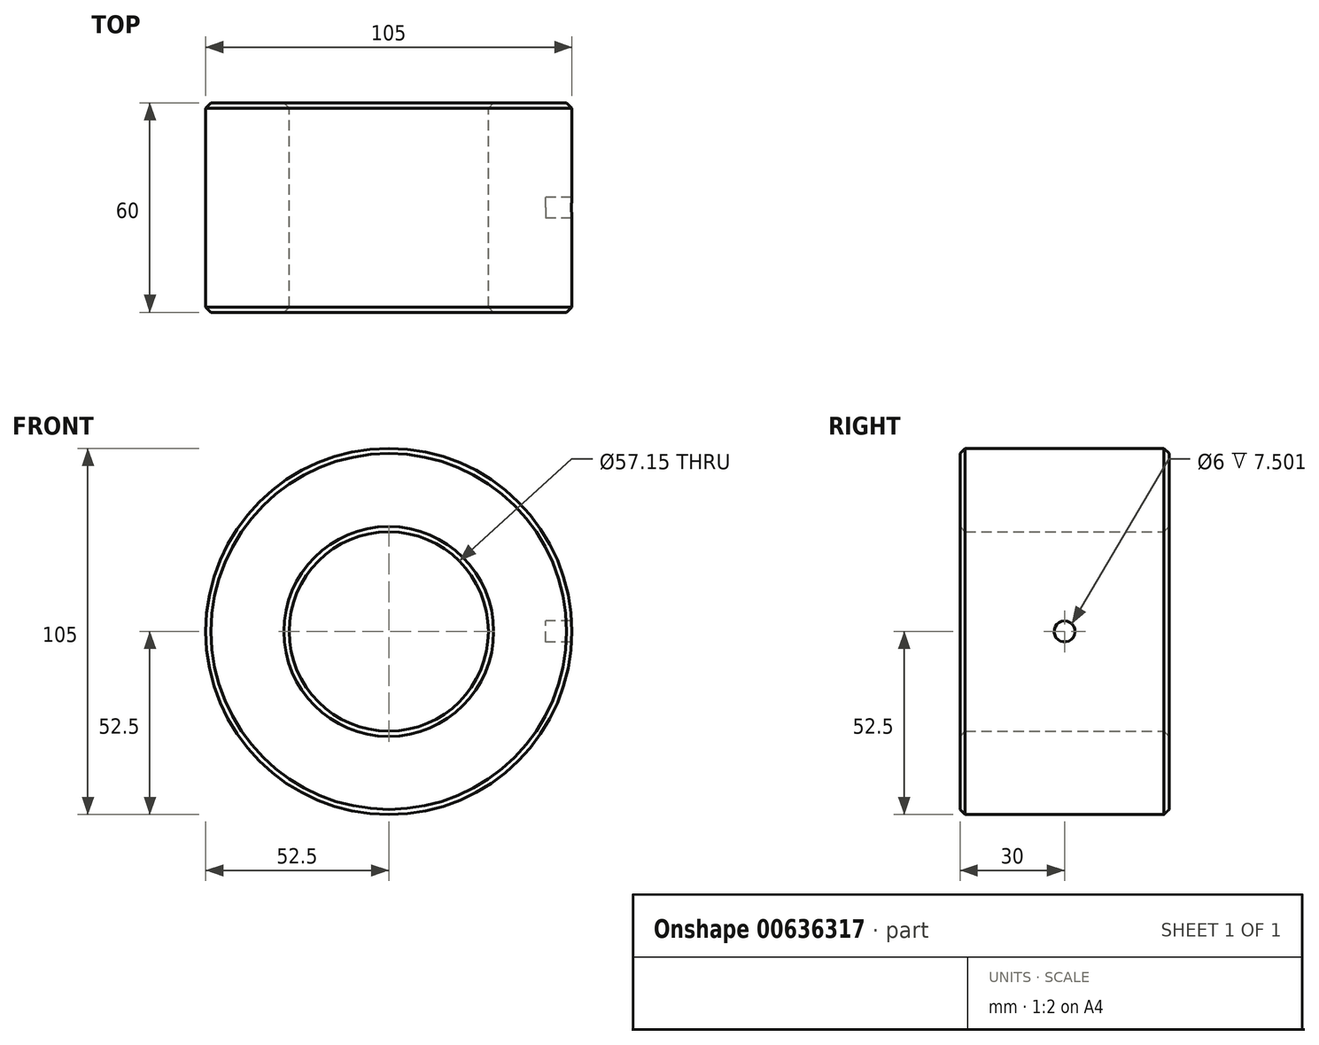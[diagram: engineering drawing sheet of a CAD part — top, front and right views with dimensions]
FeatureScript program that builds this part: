
annotation { "Feature Type Name" : "Feature", "Feature Type Description" : "" }
export const myFeature = defineFeature(function(context is Context, id is Id, definition is map)
    precondition{}
    {
        {
            var Q0;
            Q0=qCreatedBy(makeId("Front.planeOp"),FACE);
            var sketch = newSketch(context, id + "F0", { "sketchPlane" : qUnion([Q0])});
            skCircle(sketch, "E0", {"center": v(0, 0) * mm, "radius": 52.5 * mm});
            skCircle(sketch, "E1", {"center": v(0, 0) * mm, "radius": 28.57 * mm});
            skSolve(sketch);
        }
        {
            var Q0;
            Q0=makeQuery(id+"F0.imprint","IMPRINT",FACE,{"disambiguationData":[TD([[makeQuery(id+"F0.imprint","IMPRINT",EDGE,{"derivedFrom":sQuery(id+"F0.wireOp",EDGE,"E0")}),1.0]])]});
            extrude(context, id + "F1", {"entities" : qUnion([Q0]), "depth" : 60 * mm, "offsetDistance" : 25 * mm});
        }
        {
            var Q0;
            Q0=makeQuery(id+"F1.opExtrude","CAP_EDGE",EDGE,{"disambiguationData":[OSD([sQuery(id+"F0.wireOp",EDGE,"E0")])],"isStart":false});
            var Q1;
            Q1=makeQuery(id+"F1.opExtrude","CAP_EDGE",EDGE,{"disambiguationData":[OSD([sQuery(id+"F0.wireOp",EDGE,"E1")])],"isStart":false});
            var Q2;
            Q2=makeQuery(id+"F1.opExtrude","CAP_EDGE",EDGE,{"disambiguationData":[OSD([sQuery(id+"F0.wireOp",EDGE,"E0")])],"isStart":true});
            var Q3;
            Q3=makeQuery(id+"F1.opExtrude","CAP_EDGE",EDGE,{"disambiguationData":[OSD([sQuery(id+"F0.wireOp",EDGE,"E1")])],"isStart":true});
            chamfer(context, id + "F2", {"entities" : qUnion([Q0, Q1, Q2, Q3]), "width" : 1.5 * mm, "tangentPropagation" : true});
        }
        {
            var Q0;
            Q0=qCreatedBy(makeId("Right.planeOp"),FACE);
            var sketch = newSketch(context, id + "F3", { "sketchPlane" : qUnion([Q0])});
            skCircle(sketch, "E2", {"center": v(-30, 0) * mm, "radius": 3 * mm});
            skSolve(sketch);
        }
        {
            var Q0;
            Q0 = qSketchRegion(id + "F3", true);
            extrude(context, id + "F4", {"entities" : qUnion([Q0]), "operationType" : NewBodyOperationType.REMOVE, "depth" : 55 * mm, "offsetDistance" : 25 * mm, "hasSecondDirection" : true, "secondDirectionOppositeDirection" : true, "secondDirectionDepth" : -45 * mm});
        }
    });
